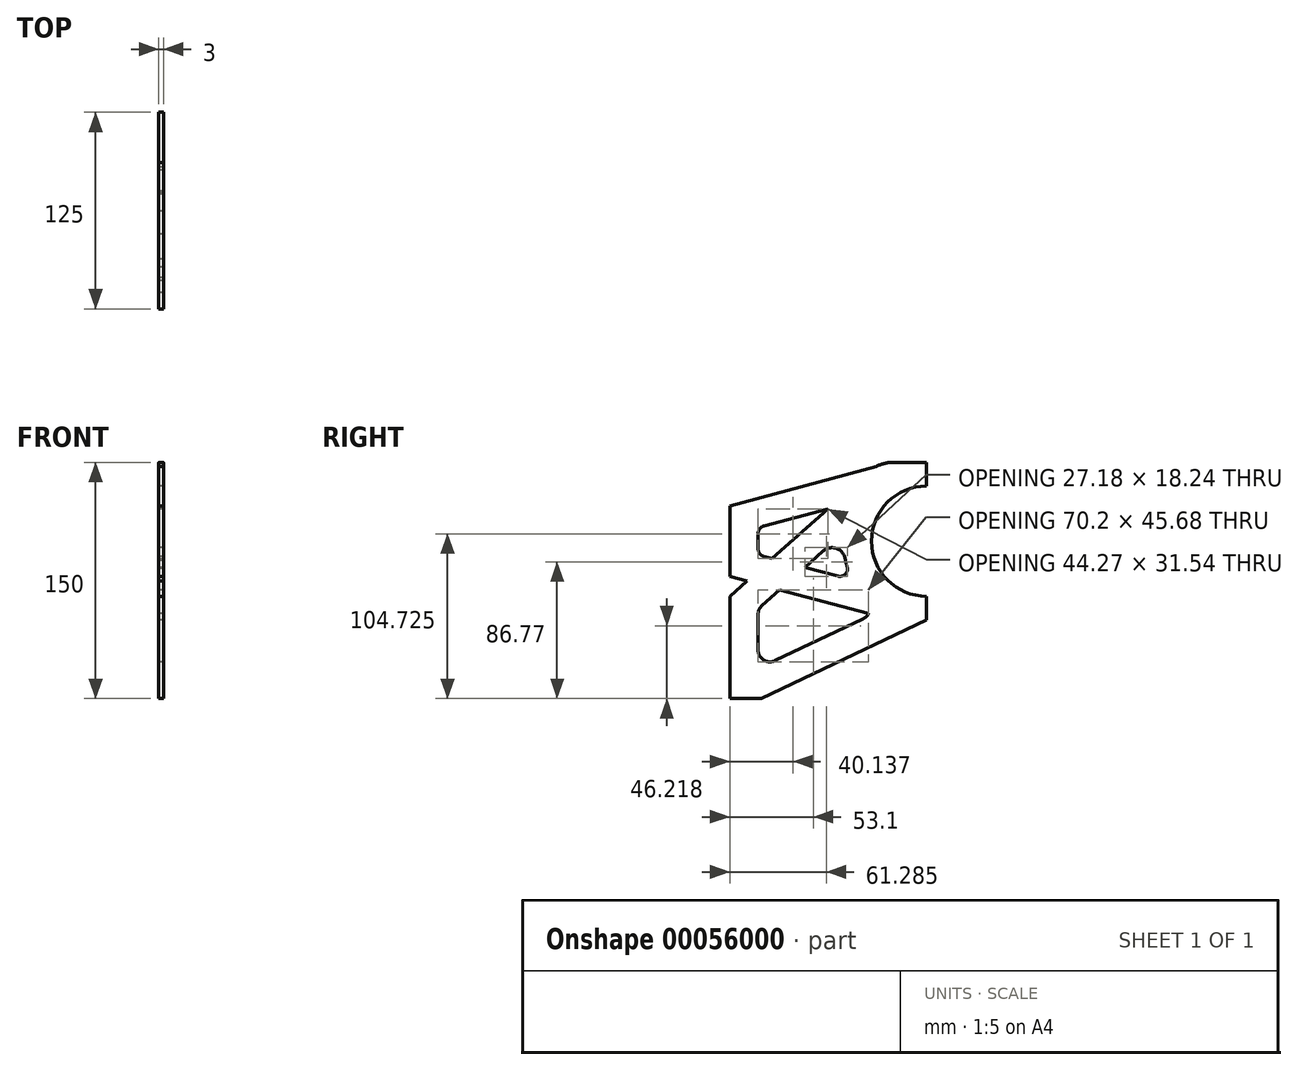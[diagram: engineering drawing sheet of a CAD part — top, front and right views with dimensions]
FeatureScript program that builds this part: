
annotation { "Feature Type Name" : "Feature", "Feature Type Description" : "" }
export const myFeature = defineFeature(function(context is Context, id is Id, definition is map)
    precondition{}
    {
        {
            var Q0;
            Q0=qCreatedBy(makeId("Right.planeOp"),FACE);
            var sketch = newSketch(context, id + "F0", { "sketchPlane" : qUnion([Q0])});
            skArc(sketch, "E0", {"start": v(0, 35) * mm, "mid": v(-35, 0) * mm, "end": v(0, -35) * mm});
            skLineSegment(sketch, "E1", {"start": v(0, 35) * mm, "end": v(0, 50) * mm});
            skLineSegment(sketch, "E2", {"start": v(0, 50) * mm, "end": v(-22, 50) * mm});
            skLineSegment(sketch, "E3", {"start": v(-35.3, 44.93) * mm, "end": v(-125, -35) * mm});
            skLineSegment(sketch, "E4", {"start": v(-125, -35) * mm, "end": v(-125, -100) * mm});
            skLineSegment(sketch, "E5", {"start": v(-125, -100) * mm, "end": v(-105, -100) * mm});
            skLineSegment(sketch, "E6", {"start": v(0, -50) * mm, "end": v(0, -35) * mm});
            skPoint(sketch, "E7.visualSharp", {"position": v(-29.62, 50) * mm});
            skArc(sketch, "E7.filletArc", {"start": v(-22, 50) * mm, "mid": v(-29.12, 48.69) * mm, "end": v(-35.3, 44.93) * mm});
            skLineSegment(sketch, "E8", {"start": v(0, -50) * mm, "end": v(-105, -100) * mm});
            skCircle(sketch, "E9", {"center": v(-99.5, -69.14) * mm, "radius": 7.5 * mm});
            skCircle(sketch, "E10", {"center": v(-60.04, -12.61) * mm, "radius": 8.5 * mm});
            skCircle(sketch, "E11", {"center": v(-44.06, -41.63) * mm, "radius": 8.5 * mm});
            skLineSegment(sketch, "E12", {"start": v(-96.28, -75.9) * mm, "end": v(-40.4, -49.3) * mm});
            skCircle(sketch, "E13", {"center": v(-99.5, -46.43) * mm, "radius": 7.5 * mm});
            skLineSegment(sketch, "E14", {"start": v(-107, -46.43) * mm, "end": v(-107, -69.14) * mm});
            skLineSegment(sketch, "E15", {"start": v(-104.49, -40.83) * mm, "end": v(-65.7, -6.26) * mm});
            skArc(sketch, "E16", {"start": v(-51.68, -11.11) * mm, "mid": v(-47, -24.34) * mm, "end": v(-38.32, -35.36) * mm});
            skSolve(sketch);
        }
        {
            var Q0;
            Q0 = qSketchRegion(id + "F0", true);
            extrude(context, id + "F1", {"entities" : qUnion([Q0]), "depth" : 3 * mm});
        }
        {
            var Q0;
            Q0=qCreatedBy(makeId("Right.planeOp"),FACE);
            var sketch = newSketch(context, id + "F2", { "sketchPlane" : qUnion([Q0])});
            skArc(sketch, "E17", {"start": v(0, 35) * mm, "mid": v(-35, 0) * mm, "end": v(0, -35) * mm});
            skLineSegment(sketch, "E18", {"start": v(0, 35) * mm, "end": v(0, 50) * mm});
            skLineSegment(sketch, "E19", {"start": v(0, 50) * mm, "end": v(-18.72, 50) * mm});
            skLineSegment(sketch, "E20", {"start": v(-25.17, 49.15) * mm, "end": v(-125, 22.5) * mm});
            skLineSegment(sketch, "E21", {"start": v(-125, 22.5) * mm, "end": v(-125, -22.5) * mm});
            skLineSegment(sketch, "E22", {"start": v(-125, -22.5) * mm, "end": v(-25.17, -49.15) * mm});
            skLineSegment(sketch, "E23", {"start": v(-18.72, -50) * mm, "end": v(0, -50) * mm});
            skLineSegment(sketch, "E24", {"start": v(0, -50) * mm, "end": v(0, -35) * mm});
            skPoint(sketch, "E25.visualSharp", {"position": v(-22, 50) * mm});
            skArc(sketch, "E25.filletArc", {"start": v(-18.72, 50) * mm, "mid": v(-21.97, 49.79) * mm, "end": v(-25.17, 49.15) * mm});
            skPoint(sketch, "E26.visualSharp", {"position": v(-22, -50) * mm});
            skArc(sketch, "E26.filletArc", {"start": v(-25.17, -49.15) * mm, "mid": v(-21.97, -49.79) * mm, "end": v(-18.72, -50) * mm});
            skLineSegment(sketch, "E27", {"start": v(-56.18, 22.24) * mm, "end": v(-103.29, 9.67) * mm});
            skLineSegment(sketch, "E28", {"start": v(-107, 4.84) * mm, "end": v(-107, -4.84) * mm});
            skLineSegment(sketch, "E29", {"start": v(-103.29, -9.67) * mm, "end": v(-56.41, -22.18) * mm});
            skArc(sketch, "E30", {"start": v(-50.2, 15.71) * mm, "mid": v(-53, 0.02) * mm, "end": v(-50.4, -15.71) * mm});
            skPoint(sketch, "E31.visualSharp", {"position": v(-107, 8.68) * mm});
            skArc(sketch, "E31.filletArc", {"start": v(-103.29, 9.67) * mm, "mid": v(-105.97, 7.88) * mm, "end": v(-107, 4.84) * mm});
            skPoint(sketch, "E32.visualSharp", {"position": v(-107, -8.68) * mm});
            skArc(sketch, "E32.filletArc", {"start": v(-107, -4.84) * mm, "mid": v(-105.97, -7.88) * mm, "end": v(-103.29, -9.67) * mm});
            skPoint(sketch, "E33.visualSharp", {"position": v(-45.57, 25.08) * mm});
            skArc(sketch, "E33.filletArc", {"start": v(-50.2, 15.71) * mm, "mid": v(-51.2, 20.8) * mm, "end": v(-56.18, 22.24) * mm});
            skPoint(sketch, "E34.visualSharp", {"position": v(-46.01, -24.96) * mm});
            skArc(sketch, "E34.filletArc", {"start": v(-56.41, -22.18) * mm, "mid": v(-51.46, -20.75) * mm, "end": v(-50.4, -15.71) * mm});
            skSolve(sketch);
        }
        {
            var Q0;
            Q0 = qSketchRegion(id + "F2", true);
            extrude(context, id + "F3", {"entities" : qUnion([Q0]), "operationType" : NewBodyOperationType.ADD, "depth" : 3 * mm});
        }
    });
